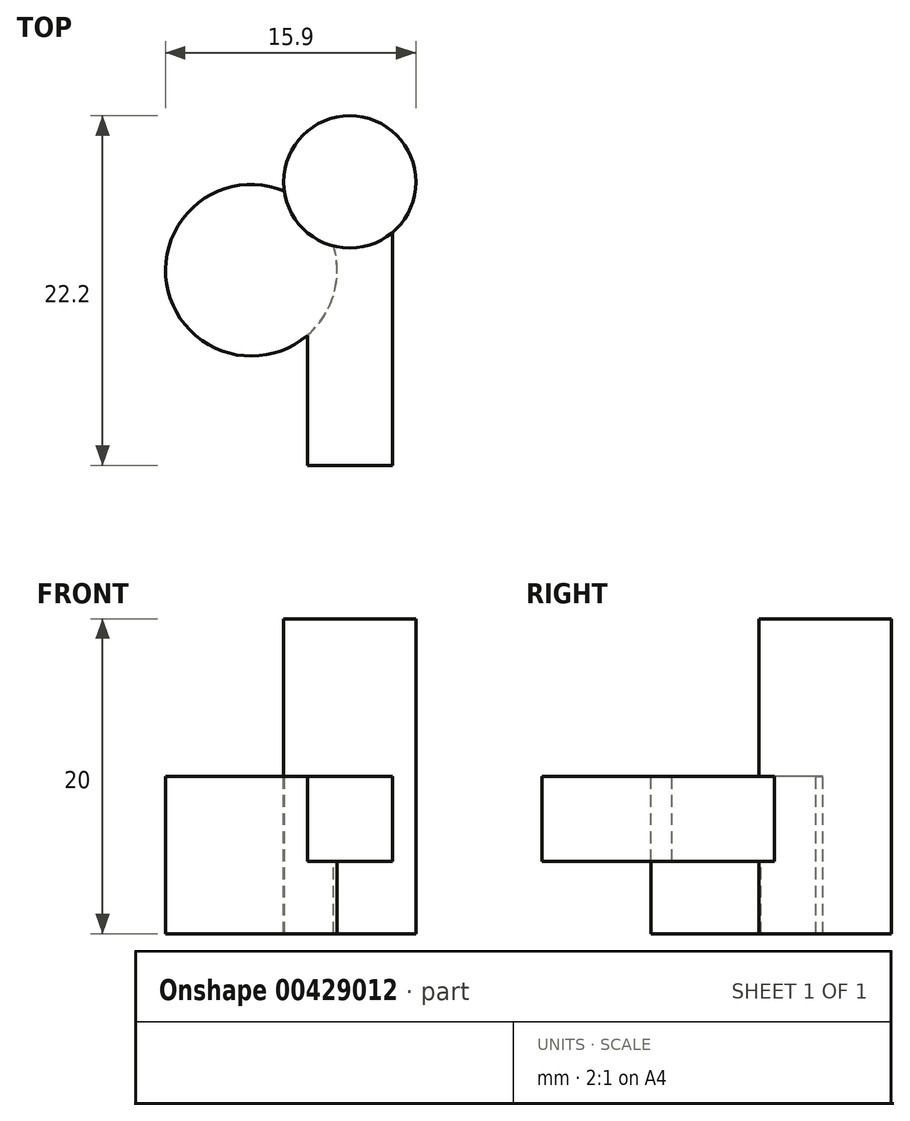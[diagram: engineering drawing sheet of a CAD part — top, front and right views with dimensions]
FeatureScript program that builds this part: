
annotation { "Feature Type Name" : "Feature", "Feature Type Description" : "" }
export const myFeature = defineFeature(function(context is Context, id is Id, definition is map)
    precondition{}
    {
        {
            var Q0;
            Q0=qCreatedBy(makeId("Top.planeOp"),FACE);
            var sketch = newSketch(context, id + "F0", { "sketchPlane" : qUnion([Q0])});
            skCircle(sketch, "E0", {"center": v(0, 0) * mm, "radius": 1.5 * mm, "construction": true});
            skCircle(sketch, "E1", {"center": v(0, 0) * mm, "radius": 3 * mm, "construction": true});
            skCircle(sketch, "E2", {"center": v(-6.25, -5.61) * mm, "radius": 4.25 * mm, "construction": true});
            skLineSegment(sketch, "E3", {"start": v(0, 0) * mm, "end": v(-6.25, -5.61) * mm, "construction": true});
            skLineSegment(sketch, "E4.bottom", {"start": v(1.5, 0) * mm, "end": v(-1.5, 0) * mm, "construction": true});
            skLineSegment(sketch, "E4.top", {"start": v(1.5, -24.87) * mm, "end": v(-1.5, -24.87) * mm, "construction": true});
            skLineSegment(sketch, "E4.left", {"start": v(1.5, 0) * mm, "end": v(1.5, -24.87) * mm, "construction": true});
            skLineSegment(sketch, "E4.right", {"start": v(-1.5, 0) * mm, "end": v(-1.5, -24.87) * mm, "construction": true});
            skLineSegment(sketch, "E5", {"start": v(-1.5, -5.61) * mm, "end": v(-2, -5.61) * mm, "construction": true});
            skLineSegment(sketch, "E6", {"start": v(-6.25, -5.61) * mm, "end": v(-3.41, -8.77) * mm, "construction": true});
            skSolve(sketch);
        }
        {
            var Q0;
            Q0=qCreatedBy(makeId("Top.planeOp"),FACE);
            var sketch = newSketch(context, id + "F1", { "sketchPlane" : qUnion([Q0])});
            skCircle(sketch, "E7.0", {"center": v(0, 0) * mm, "radius": 4.2 * mm});
            skSolve(sketch);
        }
        {
            var Q0;
            Q0=qCreatedBy(makeId("Top.planeOp"),FACE);
            var sketch = newSketch(context, id + "F2", { "sketchPlane" : qUnion([Q0])});
            skCircle(sketch, "E8.0", {"center": v(-6.25, -5.61) * mm, "radius": 5.45 * mm});
            skSolve(sketch);
        }
        {
            var Q0;
            Q0=sQuery(id+"F0.wireOp",VERTEX,"E2.center");
            var Q1;
            Q1=sQuery(id+"F0.wireOp",EDGE,"E6");
            cPlane(context, id + "F3", {"entities" : qUnion([Q0, Q1]), "cplaneType" : CPlaneType.LINE_POINT, "offset" : 25 * mm, "width" : 150 * mm, "height" : 150 * mm});
        }
        {
            var Q0;
            Q0=qCreatedBy(id+"F3.planeOp",FACE);
            var sketch = newSketch(context, id + "F4", { "sketchPlane" : qUnion([Q0])});
            skLineSegment(sketch, "E9.0", {"start": v(0, 0) * mm, "end": v(-8.4, 0) * mm, "construction": true});
            skLineSegment(sketch, "E10", {"start": v(-8.4, 0) * mm, "end": v(-8.4, 10) * mm});
            skLineSegment(sketch, "E11", {"start": v(0, 0) * mm, "end": v(0, 20) * mm});
            skSolve(sketch);
        }
        {
            var Q0;
            Q0 = qSketchRegion(id + "F1", true);
            var Q1;
            Q1=sQuery(id+"F4.wireOp",EDGE,"E11");
            sweep(context, id + "F5", {"profiles" : qUnion([Q0]), "path" : qUnion([Q1])});
        }
        {
            var Q0;
            Q0 = qSketchRegion(id + "F2", true);
            var Q1;
            Q1=sQuery(id+"F4.wireOp",EDGE,"E10");
            sweep(context, id + "F6", {"operationType" : NewBodyOperationType.ADD, "profiles" : qUnion([Q0]), "path" : qUnion([Q1])});
        }
        {
            var Q0;
            Q0=makeQuery(id+"F6.opSweep","CAP_FACE",FACE,{"disambiguationData":[OSD([sQuery(id+"F2.wireOp",EDGE,"E8.0"),sQuery(id+"F4.wireOp",VERTEX,"E10.end")])],"isStart":false});
            var sketch = newSketch(context, id + "F7", { "sketchPlane" : qUnion([Q0])});
            skLineSegment(sketch, "E12.0", {"start": v(-2.7, 1.2) * mm, "end": v(-2.7, -24.87) * mm});
            skLineSegment(sketch, "E12.1", {"start": v(2.7, 1.2) * mm, "end": v(-2.7, 1.2) * mm});
            skLineSegment(sketch, "E12.2", {"start": v(2.7, 1.2) * mm, "end": v(2.7, -24.87) * mm});
            skLineSegment(sketch, "E13", {"start": v(-2.7, -18) * mm, "end": v(2.7, -18) * mm});
            skSolve(sketch);
        }
        {
            var Q0;
            Q0 = qSketchRegion(id + "F7", true);
            extrude(context, id + "F8", {"entities" : qUnion([Q0]), "operationType" : NewBodyOperationType.ADD, "oppositeDirection" : true, "depth" : (3 + 2.4) * mm});
        }
    });
